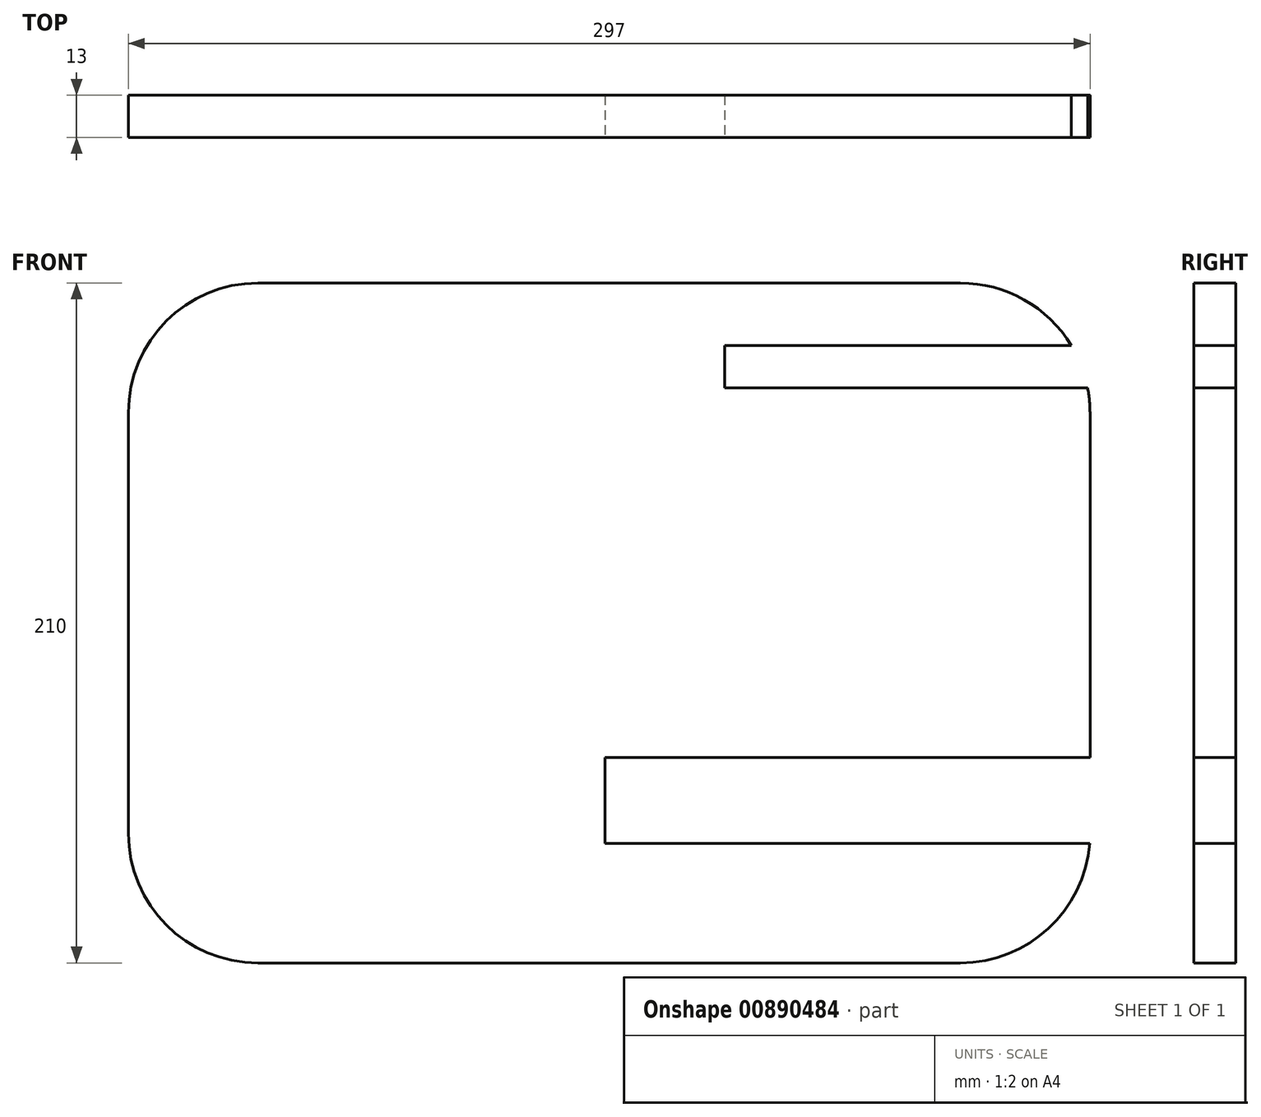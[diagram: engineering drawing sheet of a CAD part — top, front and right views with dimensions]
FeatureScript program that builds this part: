
annotation { "Feature Type Name" : "Feature", "Feature Type Description" : "" }
export const myFeature = defineFeature(function(context is Context, id is Id, definition is map)
    precondition{}
    {
        {
            var Q0;
            Q0=qCreatedBy(makeId("Front.planeOp"),FACE);
            var sketch = newSketch(context, id + "F0", { "sketchPlane" : qUnion([Q0])});
            skLineSegment(sketch, "E0.bottom", {"start": v(-107.18, 142.31) * mm, "end": v(109.82, 142.31) * mm});
            skLineSegment(sketch, "E0.top", {"start": v(-107.18, -67.69) * mm, "end": v(109.82, -67.69) * mm});
            skLineSegment(sketch, "E0.left", {"start": v(-147.18, 102.31) * mm, "end": v(-147.18, -27.69) * mm});
            skLineSegment(sketch, "E0.right", {"start": v(149.82, 102.31) * mm, "end": v(149.82, -27.69) * mm});
            skPoint(sketch, "E1.visualSharp", {"position": v(-147.18, 142.31) * mm});
            skArc(sketch, "E1.filletArc", {"start": v(-107.18, 142.31) * mm, "mid": v(-135.47, 130.6) * mm, "end": v(-147.18, 102.31) * mm});
            skPoint(sketch, "E2.visualSharp", {"position": v(149.82, 142.31) * mm});
            skArc(sketch, "E2.filletArc", {"start": v(149.82, 102.31) * mm, "mid": v(138.1, 130.6) * mm, "end": v(109.82, 142.31) * mm});
            skPoint(sketch, "E3.visualSharp", {"position": v(149.82, -67.69) * mm});
            skArc(sketch, "E3.filletArc", {"start": v(109.82, -67.69) * mm, "mid": v(138.1, -55.97) * mm, "end": v(149.82, -27.69) * mm});
            skPoint(sketch, "E4.visualSharp", {"position": v(-147.18, -67.69) * mm});
            skArc(sketch, "E4.filletArc", {"start": v(-147.18, -27.69) * mm, "mid": v(-135.47, -55.97) * mm, "end": v(-107.18, -67.69) * mm});
            skSolve(sketch);
        }
        {
            var Q0;
            Q0 = qSketchRegion(id + "F0", true);
            extrude(context, id + "F1", {"entities" : qUnion([Q0]), "depth" : 13 * mm, "offsetDistance" : 25 * mm});
        }
        {
            var Q0;
            Q0=makeQuery(id+"F1.opExtrude","CAP_FACE",FACE,{"disambiguationData":[OSD([sQuery(id+"F0.wireOp",EDGE,"E0.bottom"),sQuery(id+"F0.wireOp",EDGE,"E0.top"),sQuery(id+"F0.wireOp",EDGE,"E0.left"),sQuery(id+"F0.wireOp",EDGE,"E0.right"),sQuery(id+"F0.wireOp",EDGE,"E1.filletArc"),sQuery(id+"F0.wireOp",EDGE,"E2.filletArc"),sQuery(id+"F0.wireOp",EDGE,"E3.filletArc"),sQuery(id+"F0.wireOp",EDGE,"E4.filletArc")])],"isStart":false});
            var sketch = newSketch(context, id + "F2", { "sketchPlane" : qUnion([Q0])});
            skLineSegment(sketch, "E5.bottom", {"start": v(149.82, -4.2) * mm, "end": v(0, -4.2) * mm});
            skLineSegment(sketch, "E5.top", {"start": v(149.82, -30.8) * mm, "end": v(0, -30.8) * mm});
            skLineSegment(sketch, "E5.left", {"start": v(149.82, -4.2) * mm, "end": v(149.82, -30.8) * mm});
            skLineSegment(sketch, "E5.right", {"start": v(0, -4.2) * mm, "end": v(0, -30.8) * mm});
            skSolve(sketch);
        }
        {
            var Q0;
            {var subQ3=sQuery(id+"F2.wireOp",EDGE,"E5.bottom");Q0=makeQuery(id+"F2.imprint","IMPRINT",FACE,{"disambiguationData":[TD([[makeQuery(id+"F2.imprint","IMPRINT",EDGE,{"derivedFrom":subQ3}),1.0]])]});}
            extrude(context, id + "F3", {"entities" : qUnion([Q0]), "operationType" : NewBodyOperationType.REMOVE, "oppositeDirection" : true, "depth" : 25 * mm, "offsetDistance" : 25 * mm});
        }
        {
            var Q0;
            Q0=makeQuery(id+"F1.opExtrude","CAP_FACE",FACE,{"disambiguationData":[OSD([sQuery(id+"F0.wireOp",EDGE,"E0.bottom"),sQuery(id+"F0.wireOp",EDGE,"E0.top"),sQuery(id+"F0.wireOp",EDGE,"E0.left"),sQuery(id+"F0.wireOp",EDGE,"E0.right"),sQuery(id+"F0.wireOp",EDGE,"E1.filletArc"),sQuery(id+"F0.wireOp",EDGE,"E2.filletArc"),sQuery(id+"F0.wireOp",EDGE,"E3.filletArc"),sQuery(id+"F0.wireOp",EDGE,"E4.filletArc")])],"isStart":false});
            var sketch = newSketch(context, id + "F4", { "sketchPlane" : qUnion([Q0])});
            skLineSegment(sketch, "E6.bottom", {"start": v(149.08, 109.96) * mm, "end": v(36.96, 109.96) * mm});
            skLineSegment(sketch, "E6.top", {"start": v(149.08, 123.02) * mm, "end": v(36.96, 123.02) * mm});
            skLineSegment(sketch, "E6.left", {"start": v(149.08, 109.96) * mm, "end": v(149.08, 123.02) * mm});
            skLineSegment(sketch, "E6.right", {"start": v(36.96, 109.96) * mm, "end": v(36.96, 123.02) * mm});
            skSolve(sketch);
        }
        {
            var Q0;
            {var subQ0=sQuery(id+"F4.wireOp",EDGE,"E6.bottom");Q0=makeQuery(id+"F4.imprint","IMPRINT",FACE,{"disambiguationData":[TD([[makeQuery(id+"F4.imprint","IMPRINT",EDGE,{"derivedFrom":subQ0}),-1.0]])]});}
            extrude(context, id + "F5", {"entities" : qUnion([Q0]), "operationType" : NewBodyOperationType.REMOVE, "oppositeDirection" : true, "depth" : 25 * mm, "offsetDistance" : 25 * mm});
        }
    });
